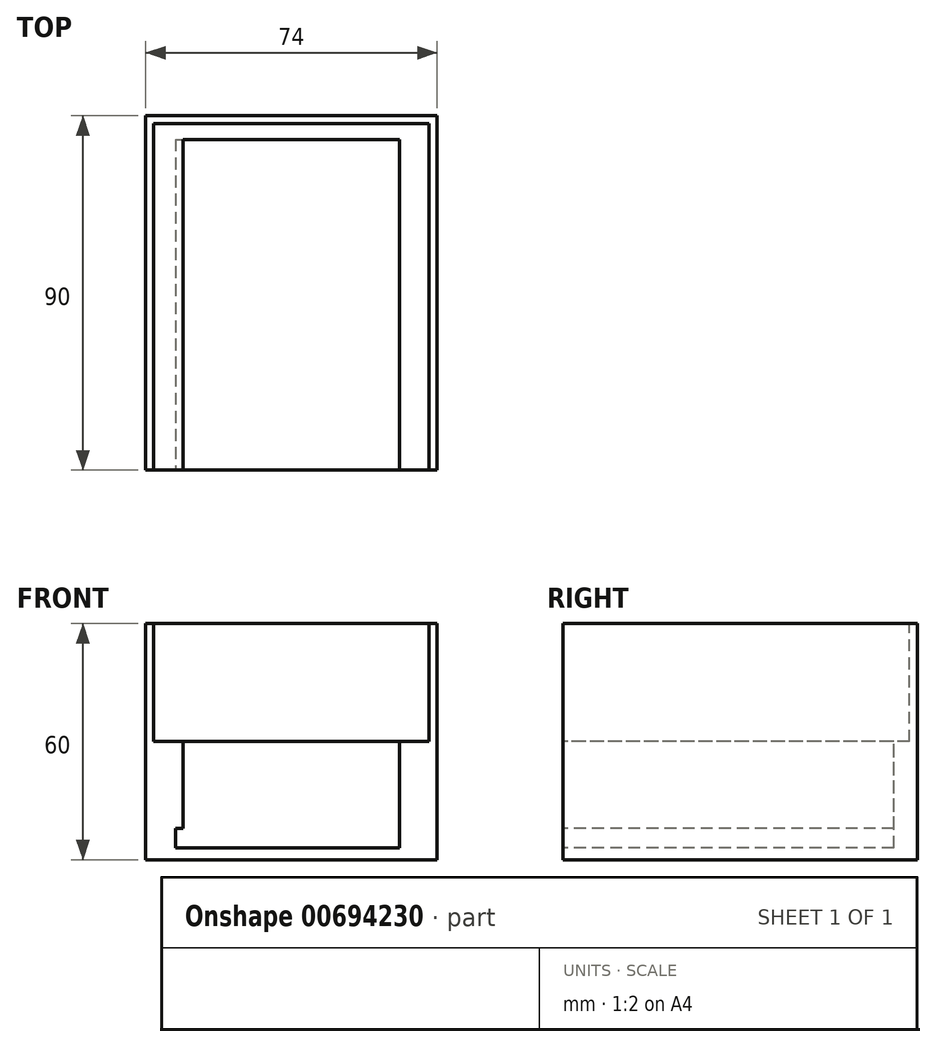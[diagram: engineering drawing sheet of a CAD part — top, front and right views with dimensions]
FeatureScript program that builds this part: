
annotation { "Feature Type Name" : "Feature", "Feature Type Description" : "" }
export const myFeature = defineFeature(function(context is Context, id is Id, definition is map)
    precondition{}
    {
        {
            var Q0;
            Q0=qCreatedBy(makeId("Top.planeOp"),FACE);
            var sketch = newSketch(context, id + "F0", { "sketchPlane" : qUnion([Q0])});
            skLineSegment(sketch, "E0.bottom", {"start": v(0, 0) * mm, "end": v(74, 0) * mm});
            skLineSegment(sketch, "E0.top", {"start": v(0, -90) * mm, "end": v(74, -90) * mm});
            skLineSegment(sketch, "E0.left", {"start": v(0, 0) * mm, "end": v(0, -90) * mm});
            skLineSegment(sketch, "E0.right", {"start": v(74, 0) * mm, "end": v(74, -90) * mm});
            skSolve(sketch);
        }
        {
            var Q0;
            Q0=makeQuery(id+"F0.imprint","IMPRINT",FACE,{"disambiguationData":[TD([[makeQuery(id+"F0.imprint","IMPRINT",EDGE,{"derivedFrom":sQuery(id+"F0.wireOp",EDGE,"E0.bottom")}),-1.0]])]});
            extrude(context, id + "F1", {"entities" : qUnion([Q0]), "depth" : 60 * mm, "offsetDistance" : 25 * mm});
        }
        {
            var Q0;
            Q0=makeQuery(id+"F1.opExtrude","CAP_FACE",FACE,{"disambiguationData":[OSD([sQuery(id+"F0.wireOp",EDGE,"E0.bottom"),sQuery(id+"F0.wireOp",EDGE,"E0.top"),sQuery(id+"F0.wireOp",EDGE,"E0.left"),sQuery(id+"F0.wireOp",EDGE,"E0.right")])],"isStart":false});
            var sketch = newSketch(context, id + "F2", { "sketchPlane" : qUnion([Q0])});
            skLineSegment(sketch, "E1.bottom", {"start": v(2, -2) * mm, "end": v(72, -2) * mm});
            skLineSegment(sketch, "E1.top", {"start": v(2, -90) * mm, "end": v(72, -90) * mm});
            skLineSegment(sketch, "E1.left", {"start": v(2, -2) * mm, "end": v(2, -90) * mm});
            skLineSegment(sketch, "E1.right", {"start": v(72, -2) * mm, "end": v(72, -90) * mm});
            skSolve(sketch);
        }
        {
            var Q0;
            Q0=makeQuery(id+"F2.imprint","IMPRINT",FACE,{"disambiguationData":[TD([[makeQuery(id+"F2.imprint","IMPRINT",EDGE,{"derivedFrom":sQuery(id+"F2.wireOp",EDGE,"E1.bottom")}),-1.0]])]});
            extrude(context, id + "F3", {"entities" : qUnion([Q0]), "operationType" : NewBodyOperationType.REMOVE, "oppositeDirection" : true, "depth" : 30 * mm, "offsetDistance" : 25 * mm});
        }
        {
            var Q0;
            Q0=makeQuery(id+"F3.boolean.opBoolean","COPY",FACE,{"derivedFrom":makeQuery(id+"F3.opExtrude","CAP_FACE",FACE,{"disambiguationData":[OSD([sQuery(id+"F2.wireOp",EDGE,"E1.bottom"),sQuery(id+"F2.wireOp",EDGE,"E1.top"),sQuery(id+"F2.wireOp",EDGE,"E1.left"),sQuery(id+"F2.wireOp",EDGE,"E1.right")])],"isStart":false})});
            var sketch = newSketch(context, id + "F4", { "sketchPlane" : qUnion([Q0])});
            skLineSegment(sketch, "E2.bottom", {"start": v(9.5, -6) * mm, "end": v(64.5, -6) * mm});
            skLineSegment(sketch, "E2.top", {"start": v(9.5, -90) * mm, "end": v(64.5, -90) * mm});
            skLineSegment(sketch, "E2.left", {"start": v(9.5, -6) * mm, "end": v(9.5, -90) * mm});
            skLineSegment(sketch, "E2.right", {"start": v(64.5, -6) * mm, "end": v(64.5, -90) * mm});
            skSolve(sketch);
        }
        {
            var Q0;
            Q0 = qSketchRegion(id + "F4", true);
            extrude(context, id + "F5", {"entities" : qUnion([Q0]), "operationType" : NewBodyOperationType.REMOVE, "oppositeDirection" : true, "depth" : 27 * mm, "offsetDistance" : 25 * mm});
        }
        {
            var Q0;
            Q0=makeQuery(id+"F5.boolean.opBoolean","COPY",FACE,{"derivedFrom":makeQuery(id+"F5.opExtrude","SWEPT_FACE",FACE,{"disambiguationData":[OSD([sQuery(id+"F4.wireOp",EDGE,"E2.left")])]})});
            var sketch = newSketch(context, id + "F6", { "sketchPlane" : qUnion([Q0])});
            skLineSegment(sketch, "E3.bottom", {"start": v(-6, 3) * mm, "end": v(-90, 3) * mm});
            skLineSegment(sketch, "E3.top", {"start": v(-6, 8) * mm, "end": v(-90, 8) * mm});
            skLineSegment(sketch, "E3.left", {"start": v(-6, 3) * mm, "end": v(-6, 8) * mm});
            skLineSegment(sketch, "E3.right", {"start": v(-90, 3) * mm, "end": v(-90, 8) * mm});
            skSolve(sketch);
        }
        {
            var Q0;
            Q0 = qSketchRegion(id + "F6", true);
            extrude(context, id + "F7", {"entities" : qUnion([Q0]), "operationType" : NewBodyOperationType.REMOVE, "oppositeDirection" : true, "depth" : 2 * mm, "offsetDistance" : 25 * mm});
        }
    });
